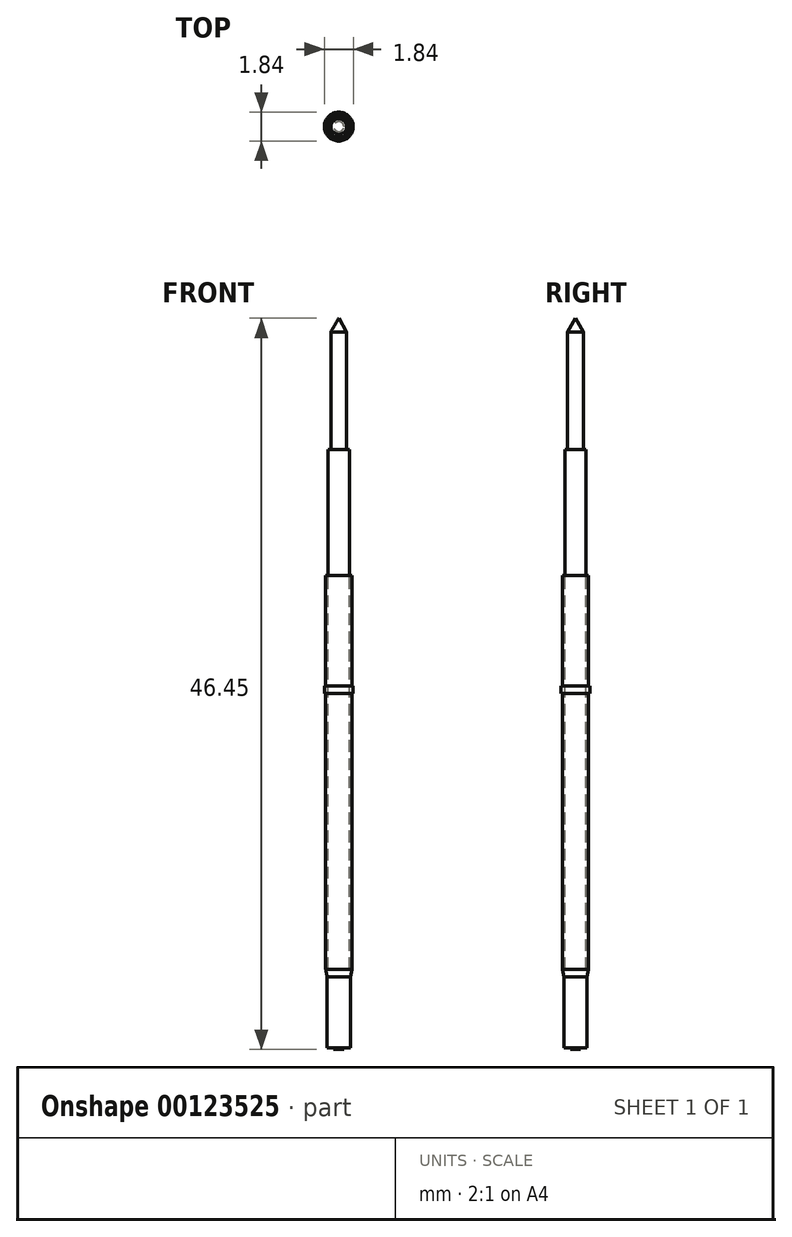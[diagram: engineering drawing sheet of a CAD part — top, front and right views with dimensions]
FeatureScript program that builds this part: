
annotation { "Feature Type Name" : "Feature", "Feature Type Description" : "" }
export const myFeature = defineFeature(function(context is Context, id is Id, definition is map)
    precondition{}
    {
        {
            var Q0;
            Q0=qCreatedBy(makeId("Front.planeOp"),FACE);
            var sketch = newSketch(context, id + "F0", { "sketchPlane" : qUnion([Q0])});
            skLineSegment(sketch, "E0", {"start": v(0, 0) * mm, "end": v(0.83, 0) * mm});
            skLineSegment(sketch, "E1", {"start": v(0.83, 0) * mm, "end": v(0.83, -7) * mm});
            skLineSegment(sketch, "E2", {"start": v(0.83, -7) * mm, "end": v(0.91, -7) * mm});
            skLineSegment(sketch, "E3", {"start": v(0.91, -7) * mm, "end": v(0.91, -7.5) * mm});
            skLineSegment(sketch, "E4", {"start": v(0.91, -7.5) * mm, "end": v(0.83, -7.5) * mm});
            skLineSegment(sketch, "E5", {"start": v(0.83, -7.5) * mm, "end": v(0.83, -25) * mm});
            skLineSegment(sketch, "E6", {"start": v(0.84, -25) * mm, "end": v(0.74, -25.5) * mm});
            skLineSegment(sketch, "E7", {"start": v(0.74, -25.5) * mm, "end": v(0.74, -30) * mm});
            skLineSegment(sketch, "E8", {"start": v(0.74, -30) * mm, "end": v(0.32, -30) * mm});
            skLineSegment(sketch, "E9", {"start": v(0.32, -30) * mm, "end": v(0.32, -30.1) * mm});
            skLineSegment(sketch, "E10", {"start": v(0.32, -30.1) * mm, "end": v(0, -30.1) * mm});
            skLineSegment(sketch, "E11", {"start": v(0, -30.1) * mm, "end": v(0, 0) * mm});
            skSolve(sketch);
        }
        {
            var Q0;
            Q0=makeQuery(id+"F0.imprint","IMPRINT",FACE,{"disambiguationData":[TD([[makeQuery(id+"F0.imprint","IMPRINT",EDGE,{"derivedFrom":sQuery(id+"F0.wireOp",EDGE,"E0")}),-1.0]])]});
            var Q1;
            Q1=sQuery(id+"F0.wireOp",EDGE,"E11");
            revolve(context, id + "F1", {"entities" : qUnion([Q0]), "axis" : qUnion([Q1]), "revolveType" : RevolveType.FULL});
        }
        {
            var Q0;
            Q0=qCreatedBy(makeId("Right.planeOp"),FACE);
            var sketch = newSketch(context, id + "F2", { "sketchPlane" : qUnion([Q0])});
            skLineSegment(sketch, "E12", {"start": v(0, 0) * mm, "end": v(0, -25) * mm});
            skLineSegment(sketch, "E13", {"start": v(0, -25) * mm, "end": v(-0.68, -25) * mm});
            skLineSegment(sketch, "E14", {"start": v(-0.68, -25) * mm, "end": v(-0.68, 8) * mm});
            skLineSegment(sketch, "E15", {"start": v(0, 16.35) * mm, "end": v(0, 0) * mm});
            skLineSegment(sketch, "E16", {"start": v(-0.68, 8) * mm, "end": v(-0.5, 8) * mm});
            skLineSegment(sketch, "E17", {"start": v(-0.5, 8) * mm, "end": v(-0.5, 15.48) * mm});
            skLineSegment(sketch, "E18", {"start": v(-0.5, 15.48) * mm, "end": v(0, 16.35) * mm});
            skSolve(sketch);
        }
        {
            var Q0;
            Q0=makeQuery(id+"F2.imprint","IMPRINT",FACE,{"disambiguationData":[TD([[makeQuery(id+"F2.imprint","IMPRINT",EDGE,{"derivedFrom":sQuery(id+"F2.wireOp",EDGE,"E12")}),-1.0]])]});
            var Q1;
            Q1=sQuery(id+"F2.wireOp",EDGE,"E15");
            revolve(context, id + "F3", {"entities" : qUnion([Q0]), "axis" : qUnion([Q1]), "revolveType" : RevolveType.FULL});
        }
    });
